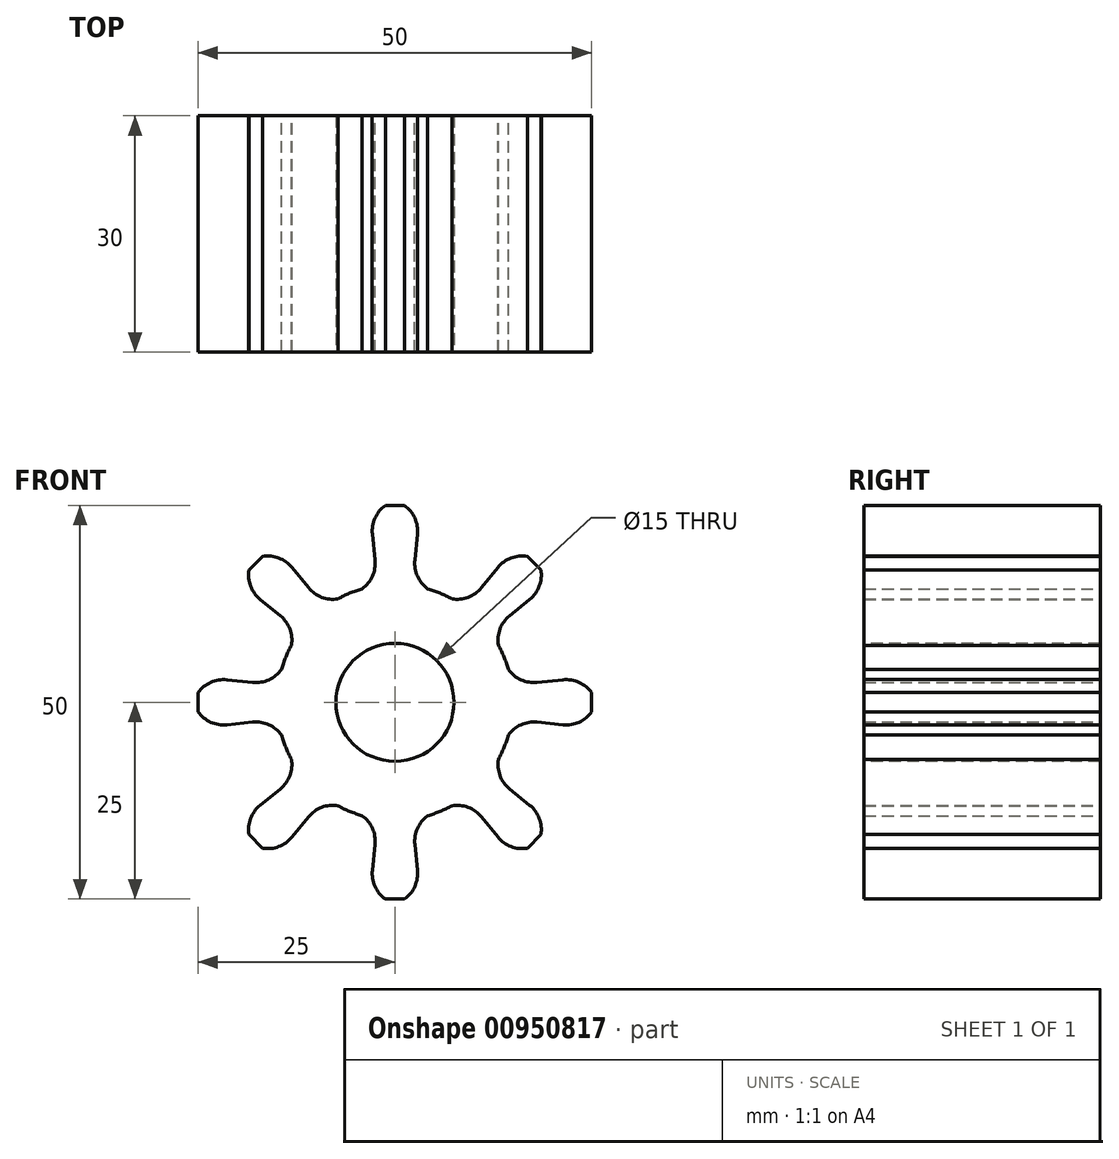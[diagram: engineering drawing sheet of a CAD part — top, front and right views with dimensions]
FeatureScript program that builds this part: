
annotation { "Feature Type Name" : "Feature", "Feature Type Description" : "" }
export const myFeature = defineFeature(function(context is Context, id is Id, definition is map)
    precondition{}
    {
        {
            var Q0;
            Q0=qCreatedBy(makeId("Front.planeOp"),FACE);
            var sketch = newSketch(context, id + "F0", { "sketchPlane" : qUnion([Q0])});
            skArc(sketch, "E0", {"start": v(-13.14, 7.24) * mm, "mid": v(-13.86, 5.74) * mm, "end": v(-14.4, 4.17) * mm});
            skArc(sketch, "E1", {"start": v(-4.17, 14.4) * mm, "mid": v(-2.86, 16.01) * mm, "end": v(-2.53, 18.06) * mm});
            skLineSegment(sketch, "E2", {"start": v(-2.53, 18.06) * mm, "end": v(-2.86, 21.35) * mm});
            skLineSegment(sketch, "E3", {"start": v(-1.22, 25) * mm, "end": v(1.22, 25) * mm});
            skArc(sketch, "E4", {"start": v(-1.22, 25) * mm, "mid": v(-2.53, 23.4) * mm, "end": v(-2.86, 21.35) * mm});
            skArc(sketch, "E5.MirrorCS", {"start": v(1.22, 25) * mm, "mid": v(2.53, 23.4) * mm, "end": v(2.86, 21.35) * mm});
            skLineSegment(sketch, "E6.MirrorCS", {"start": v(2.53, 18.06) * mm, "end": v(2.86, 21.35) * mm});
            skArc(sketch, "E7.MirrorCS", {"start": v(4.17, 14.4) * mm, "mid": v(2.86, 16.01) * mm, "end": v(2.53, 18.06) * mm});
            skLineSegment(sketch, "E8.1.0", {"start": v(-18.54, 16.81) * mm, "end": v(-16.81, 18.54) * mm});
            skArc(sketch, "E8.1.1", {"start": v(-18.54, 16.81) * mm, "mid": v(-18.33, 14.75) * mm, "end": v(-17.12, 13.07) * mm});
            skLineSegment(sketch, "E8.1.2", {"start": v(-14.56, 10.98) * mm, "end": v(-17.12, 13.07) * mm});
            skArc(sketch, "E8.1.3", {"start": v(-13.14, 7.24) * mm, "mid": v(-13.34, 9.3) * mm, "end": v(-14.56, 10.98) * mm});
            skArc(sketch, "E8.1.4", {"start": v(-7.24, 13.14) * mm, "mid": v(-9.3, 13.34) * mm, "end": v(-10.98, 14.56) * mm});
            skLineSegment(sketch, "E8.1.5", {"start": v(-10.98, 14.56) * mm, "end": v(-13.07, 17.12) * mm});
            skArc(sketch, "E8.1.6", {"start": v(-16.81, 18.54) * mm, "mid": v(-14.75, 18.33) * mm, "end": v(-13.07, 17.12) * mm});
            skLineSegment(sketch, "E8.2.0", {"start": v(-25, -1.22) * mm, "end": v(-25, 1.22) * mm});
            skArc(sketch, "E8.2.1", {"start": v(-25, -1.22) * mm, "mid": v(-23.4, -2.53) * mm, "end": v(-21.35, -2.86) * mm});
            skLineSegment(sketch, "E8.2.2", {"start": v(-18.06, -2.53) * mm, "end": v(-21.35, -2.86) * mm});
            skArc(sketch, "E8.2.3", {"start": v(-14.4, -4.17) * mm, "mid": v(-16.01, -2.86) * mm, "end": v(-18.06, -2.53) * mm});
            skArc(sketch, "E8.2.4", {"start": v(-14.4, 4.17) * mm, "mid": v(-16.01, 2.86) * mm, "end": v(-18.06, 2.53) * mm});
            skLineSegment(sketch, "E8.2.5", {"start": v(-18.06, 2.53) * mm, "end": v(-21.35, 2.86) * mm});
            skArc(sketch, "E8.2.6", {"start": v(-25, 1.22) * mm, "mid": v(-23.4, 2.53) * mm, "end": v(-21.35, 2.86) * mm});
            skLineSegment(sketch, "E8.3.0", {"start": v(-16.81, -18.54) * mm, "end": v(-18.54, -16.81) * mm});
            skArc(sketch, "E8.3.1", {"start": v(-16.81, -18.54) * mm, "mid": v(-14.75, -18.33) * mm, "end": v(-13.07, -17.12) * mm});
            skLineSegment(sketch, "E8.3.2", {"start": v(-10.98, -14.56) * mm, "end": v(-13.07, -17.12) * mm});
            skArc(sketch, "E8.3.3", {"start": v(-7.24, -13.14) * mm, "mid": v(-9.3, -13.34) * mm, "end": v(-10.98, -14.56) * mm});
            skArc(sketch, "E8.3.4", {"start": v(-13.14, -7.24) * mm, "mid": v(-13.34, -9.3) * mm, "end": v(-14.56, -10.98) * mm});
            skLineSegment(sketch, "E8.3.5", {"start": v(-14.56, -10.98) * mm, "end": v(-17.12, -13.07) * mm});
            skArc(sketch, "E8.3.6", {"start": v(-18.54, -16.81) * mm, "mid": v(-18.33, -14.75) * mm, "end": v(-17.12, -13.07) * mm});
            skLineSegment(sketch, "E8.4.0", {"start": v(1.22, -25) * mm, "end": v(-1.22, -25) * mm});
            skArc(sketch, "E8.4.1", {"start": v(1.22, -25) * mm, "mid": v(2.53, -23.4) * mm, "end": v(2.86, -21.35) * mm});
            skLineSegment(sketch, "E8.4.2", {"start": v(2.53, -18.06) * mm, "end": v(2.86, -21.35) * mm});
            skArc(sketch, "E8.4.3", {"start": v(4.17, -14.4) * mm, "mid": v(2.86, -16.01) * mm, "end": v(2.53, -18.06) * mm});
            skArc(sketch, "E8.4.4", {"start": v(-4.17, -14.4) * mm, "mid": v(-2.86, -16.01) * mm, "end": v(-2.53, -18.06) * mm});
            skLineSegment(sketch, "E8.4.5", {"start": v(-2.53, -18.06) * mm, "end": v(-2.86, -21.35) * mm});
            skArc(sketch, "E8.4.6", {"start": v(-1.22, -25) * mm, "mid": v(-2.53, -23.4) * mm, "end": v(-2.86, -21.35) * mm});
            skLineSegment(sketch, "E8.5.0", {"start": v(18.54, -16.81) * mm, "end": v(16.81, -18.54) * mm});
            skArc(sketch, "E8.5.1", {"start": v(18.54, -16.81) * mm, "mid": v(18.33, -14.75) * mm, "end": v(17.12, -13.07) * mm});
            skLineSegment(sketch, "E8.5.2", {"start": v(14.56, -10.98) * mm, "end": v(17.12, -13.07) * mm});
            skArc(sketch, "E8.5.3", {"start": v(13.14, -7.24) * mm, "mid": v(13.34, -9.3) * mm, "end": v(14.56, -10.98) * mm});
            skArc(sketch, "E8.5.4", {"start": v(7.24, -13.14) * mm, "mid": v(9.3, -13.34) * mm, "end": v(10.98, -14.56) * mm});
            skLineSegment(sketch, "E8.5.5", {"start": v(10.98, -14.56) * mm, "end": v(13.07, -17.12) * mm});
            skArc(sketch, "E8.5.6", {"start": v(16.81, -18.54) * mm, "mid": v(14.75, -18.33) * mm, "end": v(13.07, -17.12) * mm});
            skLineSegment(sketch, "E8.6.0", {"start": v(25, 1.22) * mm, "end": v(25, -1.22) * mm});
            skArc(sketch, "E8.6.1", {"start": v(25, 1.22) * mm, "mid": v(23.4, 2.53) * mm, "end": v(21.35, 2.86) * mm});
            skLineSegment(sketch, "E8.6.2", {"start": v(18.06, 2.53) * mm, "end": v(21.35, 2.86) * mm});
            skArc(sketch, "E8.6.3", {"start": v(14.4, 4.17) * mm, "mid": v(16.01, 2.86) * mm, "end": v(18.06, 2.53) * mm});
            skArc(sketch, "E8.6.4", {"start": v(14.4, -4.17) * mm, "mid": v(16.01, -2.86) * mm, "end": v(18.06, -2.53) * mm});
            skLineSegment(sketch, "E8.6.5", {"start": v(18.06, -2.53) * mm, "end": v(21.35, -2.86) * mm});
            skArc(sketch, "E8.6.6", {"start": v(25, -1.22) * mm, "mid": v(23.4, -2.53) * mm, "end": v(21.35, -2.86) * mm});
            skLineSegment(sketch, "E8.7.0", {"start": v(16.81, 18.54) * mm, "end": v(18.54, 16.81) * mm});
            skArc(sketch, "E8.7.1", {"start": v(16.81, 18.54) * mm, "mid": v(14.75, 18.33) * mm, "end": v(13.07, 17.12) * mm});
            skLineSegment(sketch, "E8.7.2", {"start": v(10.98, 14.56) * mm, "end": v(13.07, 17.12) * mm});
            skArc(sketch, "E8.7.3", {"start": v(7.24, 13.14) * mm, "mid": v(9.3, 13.34) * mm, "end": v(10.98, 14.56) * mm});
            skArc(sketch, "E8.7.4", {"start": v(13.14, 7.24) * mm, "mid": v(13.34, 9.3) * mm, "end": v(14.56, 10.98) * mm});
            skLineSegment(sketch, "E8.7.5", {"start": v(14.56, 10.98) * mm, "end": v(17.12, 13.07) * mm});
            skArc(sketch, "E8.7.6", {"start": v(18.54, 16.81) * mm, "mid": v(18.33, 14.75) * mm, "end": v(17.12, 13.07) * mm});
            skArc(sketch, "E9.trimOffspring", {"start": v(-4.17, 14.4) * mm, "mid": v(-5.74, 13.86) * mm, "end": v(-7.24, 13.14) * mm});
            skArc(sketch, "E10.trimOffspring", {"start": v(7.24, 13.14) * mm, "mid": v(5.74, 13.86) * mm, "end": v(4.17, 14.4) * mm});
            skArc(sketch, "E11.trimOffspring", {"start": v(14.4, 4.17) * mm, "mid": v(13.86, 5.74) * mm, "end": v(13.14, 7.24) * mm});
            skArc(sketch, "E12.trimOffspring", {"start": v(13.14, -7.24) * mm, "mid": v(13.86, -5.74) * mm, "end": v(14.4, -4.17) * mm});
            skArc(sketch, "E13.trimOffspring", {"start": v(4.17, -14.4) * mm, "mid": v(5.74, -13.86) * mm, "end": v(7.24, -13.14) * mm});
            skArc(sketch, "E14.trimOffspring", {"start": v(-7.24, -13.14) * mm, "mid": v(-5.74, -13.86) * mm, "end": v(-4.17, -14.4) * mm});
            skArc(sketch, "E15.trimOffspring", {"start": v(-14.4, -4.17) * mm, "mid": v(-13.86, -5.74) * mm, "end": v(-13.14, -7.24) * mm});
            skSolve(sketch);
        }
        {
            var Q0;
            Q0=qSketchRegion(id+"F0",true);
            extrude(context, id + "F1", {"entities" : qUnion([Q0]), "depth" : 30 * mm, "offsetDistance" : 25 * mm});
        }
        {
            var Q0;
            Q0=makeQuery(id+"F1.opExtrude","CAP_FACE",FACE,{"disambiguationData":[OSD([sQuery(id+"F0.wireOp",EDGE,"E0"),sQuery(id+"F0.wireOp",EDGE,"E1"),sQuery(id+"F0.wireOp",EDGE,"E2"),sQuery(id+"F0.wireOp",EDGE,"E3"),sQuery(id+"F0.wireOp",EDGE,"E4"),sQuery(id+"F0.wireOp",EDGE,"E5.MirrorCS"),sQuery(id+"F0.wireOp",EDGE,"E6.MirrorCS"),sQuery(id+"F0.wireOp",EDGE,"E7.MirrorCS"),sQuery(id+"F0.wireOp",EDGE,"E8.1.0"),sQuery(id+"F0.wireOp",EDGE,"E8.1.1"),sQuery(id+"F0.wireOp",EDGE,"E8.1.2"),sQuery(id+"F0.wireOp",EDGE,"E8.1.3"),sQuery(id+"F0.wireOp",EDGE,"E8.1.4"),sQuery(id+"F0.wireOp",EDGE,"E8.1.5"),sQuery(id+"F0.wireOp",EDGE,"E8.1.6"),sQuery(id+"F0.wireOp",EDGE,"E8.2.0"),sQuery(id+"F0.wireOp",EDGE,"E8.2.1"),sQuery(id+"F0.wireOp",EDGE,"E8.2.2"),sQuery(id+"F0.wireOp",EDGE,"E8.2.3"),sQuery(id+"F0.wireOp",EDGE,"E8.2.4"),sQuery(id+"F0.wireOp",EDGE,"E8.2.5"),sQuery(id+"F0.wireOp",EDGE,"E8.2.6"),sQuery(id+"F0.wireOp",EDGE,"E8.3.0"),sQuery(id+"F0.wireOp",EDGE,"E8.3.1"),sQuery(id+"F0.wireOp",EDGE,"E8.3.2"),sQuery(id+"F0.wireOp",EDGE,"E8.3.3"),sQuery(id+"F0.wireOp",EDGE,"E8.3.4"),sQuery(id+"F0.wireOp",EDGE,"E8.3.5"),sQuery(id+"F0.wireOp",EDGE,"E8.3.6"),sQuery(id+"F0.wireOp",EDGE,"E8.4.0"),sQuery(id+"F0.wireOp",EDGE,"E8.4.1"),sQuery(id+"F0.wireOp",EDGE,"E8.4.2"),sQuery(id+"F0.wireOp",EDGE,"E8.4.3"),sQuery(id+"F0.wireOp",EDGE,"E8.4.4"),sQuery(id+"F0.wireOp",EDGE,"E8.4.5"),sQuery(id+"F0.wireOp",EDGE,"E8.4.6"),sQuery(id+"F0.wireOp",EDGE,"E8.5.0"),sQuery(id+"F0.wireOp",EDGE,"E8.5.1"),sQuery(id+"F0.wireOp",EDGE,"E8.5.2"),sQuery(id+"F0.wireOp",EDGE,"E8.5.3"),sQuery(id+"F0.wireOp",EDGE,"E8.5.4"),sQuery(id+"F0.wireOp",EDGE,"E8.5.5"),sQuery(id+"F0.wireOp",EDGE,"E8.5.6"),sQuery(id+"F0.wireOp",EDGE,"E8.6.0"),sQuery(id+"F0.wireOp",EDGE,"E8.6.1"),sQuery(id+"F0.wireOp",EDGE,"E8.6.2"),sQuery(id+"F0.wireOp",EDGE,"E8.6.3"),sQuery(id+"F0.wireOp",EDGE,"E8.6.4"),sQuery(id+"F0.wireOp",EDGE,"E8.6.5"),sQuery(id+"F0.wireOp",EDGE,"E8.6.6"),sQuery(id+"F0.wireOp",EDGE,"E8.7.0"),sQuery(id+"F0.wireOp",EDGE,"E8.7.1"),sQuery(id+"F0.wireOp",EDGE,"E8.7.2"),sQuery(id+"F0.wireOp",EDGE,"E8.7.3"),sQuery(id+"F0.wireOp",EDGE,"E8.7.4"),sQuery(id+"F0.wireOp",EDGE,"E8.7.5"),sQuery(id+"F0.wireOp",EDGE,"E8.7.6"),sQuery(id+"F0.wireOp",EDGE,"E9.trimOffspring"),sQuery(id+"F0.wireOp",EDGE,"E10.trimOffspring"),sQuery(id+"F0.wireOp",EDGE,"E11.trimOffspring"),sQuery(id+"F0.wireOp",EDGE,"E12.trimOffspring"),sQuery(id+"F0.wireOp",EDGE,"E13.trimOffspring"),sQuery(id+"F0.wireOp",EDGE,"E14.trimOffspring"),sQuery(id+"F0.wireOp",EDGE,"E15.trimOffspring")])],"isStart":false});
            var sketch = newSketch(context, id + "F2", { "sketchPlane" : qUnion([Q0])});
            skCircle(sketch, "E16", {"center": v(0, 0) * mm, "radius": 7.5 * mm});
            skSolve(sketch);
        }
        {
            var Q0;
            Q0=qSketchRegion(id+"F2",true);
            extrude(context, id + "F3", {"entities" : qUnion([Q0]), "operationType" : NewBodyOperationType.REMOVE, "endBound" : BoundingType.THROUGH_ALL, "oppositeDirection" : true, "depth" : 25 * mm, "offsetDistance" : 25 * mm});
        }
    });
